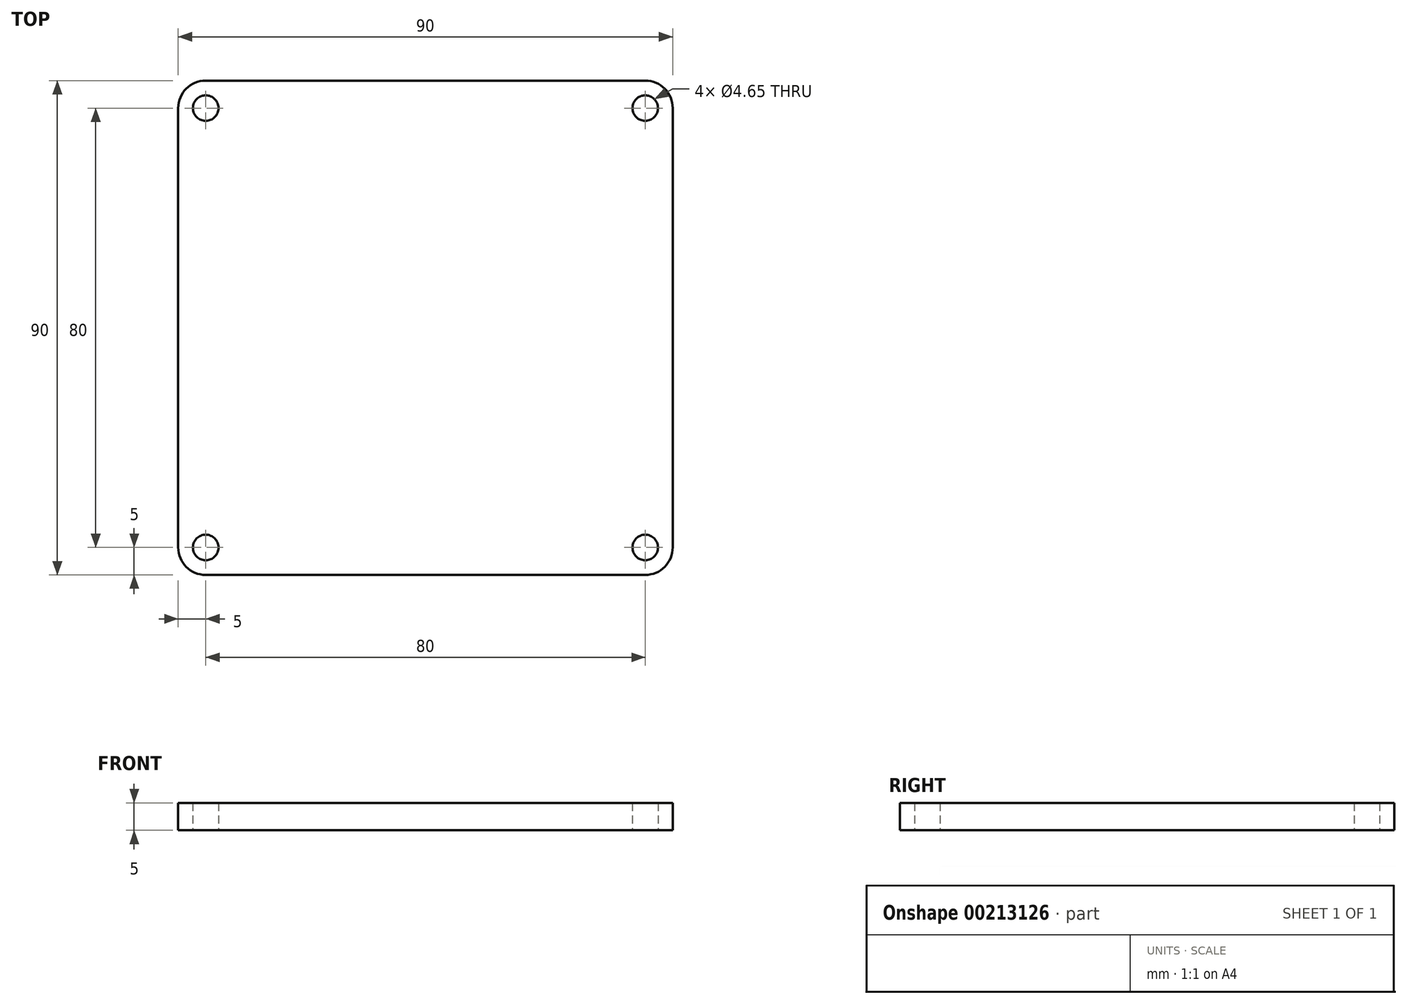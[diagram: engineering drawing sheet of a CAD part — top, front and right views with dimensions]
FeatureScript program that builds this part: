
annotation { "Feature Type Name" : "Feature", "Feature Type Description" : "" }
export const myFeature = defineFeature(function(context is Context, id is Id, definition is map)
    precondition{}
    {
        {
            var Q0;
            Q0=qCreatedBy(makeId("Top.planeOp"),FACE);
            var sketch = newSketch(context, id + "F0", { "sketchPlane" : qUnion([Q0])});
            skLineSegment(sketch, "E0.bottom", {"start": v(-40, 45) * mm, "end": v(40, 45) * mm});
            skLineSegment(sketch, "E0.top", {"start": v(-40, -45) * mm, "end": v(40, -45) * mm});
            skLineSegment(sketch, "E0.left", {"start": v(-45, 40) * mm, "end": v(-45, -40) * mm});
            skLineSegment(sketch, "E0.right", {"start": v(45, 40) * mm, "end": v(45, -40) * mm});
            skPoint(sketch, "E0.middle", {"position": v(0, 0) * mm});
            skPoint(sketch, "E1.visualSharp", {"position": v(-45, 45) * mm});
            skArc(sketch, "E1.filletArc", {"start": v(-40, 45) * mm, "mid": v(-43.54, 43.54) * mm, "end": v(-45, 40) * mm});
            skPoint(sketch, "E2.visualSharp", {"position": v(-45, -45) * mm});
            skArc(sketch, "E2.filletArc", {"start": v(-45, -40) * mm, "mid": v(-43.54, -43.54) * mm, "end": v(-40, -45) * mm});
            skPoint(sketch, "E3.visualSharp", {"position": v(45, -45) * mm});
            skArc(sketch, "E3.filletArc", {"start": v(40, -45) * mm, "mid": v(43.54, -43.54) * mm, "end": v(45, -40) * mm});
            skPoint(sketch, "E4.visualSharp", {"position": v(45, 45) * mm});
            skArc(sketch, "E4.filletArc", {"start": v(45, 40) * mm, "mid": v(43.54, 43.54) * mm, "end": v(40, 45) * mm});
            skCircle(sketch, "E5", {"center": v(40, 40) * mm, "radius": 2.33 * mm});
            skCircle(sketch, "E6", {"center": v(40, -40) * mm, "radius": 2.33 * mm});
            skCircle(sketch, "E7", {"center": v(-40, -40) * mm, "radius": 2.33 * mm});
            skCircle(sketch, "E8.MirrorC", {"center": v(-40, 40) * mm, "radius": 2.33 * mm});
            skLineSegment(sketch, "E9.bottom", {"start": v(-36.84, 39.07) * mm, "end": v(36.84, 39.07) * mm});
            skLineSegment(sketch, "E9.top", {"start": v(-36.84, -39.07) * mm, "end": v(36.84, -39.07) * mm});
            skLineSegment(sketch, "E9.left", {"start": v(-39.16, 36.74) * mm, "end": v(-39.16, -36.74) * mm});
            skLineSegment(sketch, "E9.right", {"start": v(39.16, 36.74) * mm, "end": v(39.16, -36.74) * mm});
            skArc(sketch, "E10.trimOffspring", {"start": v(-39.16, 36.74) * mm, "mid": v(-37.52, 37.42) * mm, "end": v(-36.84, 39.07) * mm});
            skArc(sketch, "E11.MirrorCS", {"start": v(-39.16, -36.74) * mm, "mid": v(-37.52, -37.42) * mm, "end": v(-36.84, -39.07) * mm});
            skArc(sketch, "E12.MirrorCS", {"start": v(39.16, 36.74) * mm, "mid": v(37.52, 37.42) * mm, "end": v(36.84, 39.07) * mm});
            skArc(sketch, "E13.MirrorCS", {"start": v(39.16, -36.74) * mm, "mid": v(37.52, -37.42) * mm, "end": v(36.84, -39.07) * mm});
            skLineSegment(sketch, "E14", {"start": v(40, 40) * mm, "end": v(43.54, 43.54) * mm, "construction": true});
            skSolve(sketch);
        }
        {
            var Q0;
            Q0 = qSketchRegion(id + "F0", true);
            var Q1;
            Q1=makeQuery(id+"F0.imprint","IMPRINT",FACE,{"disambiguationData":[TD([[makeQuery(id+"F0.imprint","IMPRINT",EDGE,{"derivedFrom":sQuery(id+"F0.wireOp",EDGE,"E9.bottom")}),-1.0]])]});
            var Q2;
            Q2=sQuery(id+"F0.wireOp",EDGE,"E9.left");
            var Q3;
            Q3=sQuery(id+"F0.wireOp",EDGE,"E9.bottom");
            var Q4;
            Q4=sQuery(id+"F0.wireOp",EDGE,"E9.right");
            var Q5;
            Q5=sQuery(id+"F0.wireOp",EDGE,"E9.top");
            var Q6;
            Q6=sQuery(id+"F0.wireOp",EDGE,"E0.bottom");
            extrude(context, id + "F1", {"entities" : qUnion([Q0, Q1]), "surfaceEntities" : qUnion([Q2, Q3, Q4, Q5, Q6]), "depth" : 5 * mm});
        }
    });
